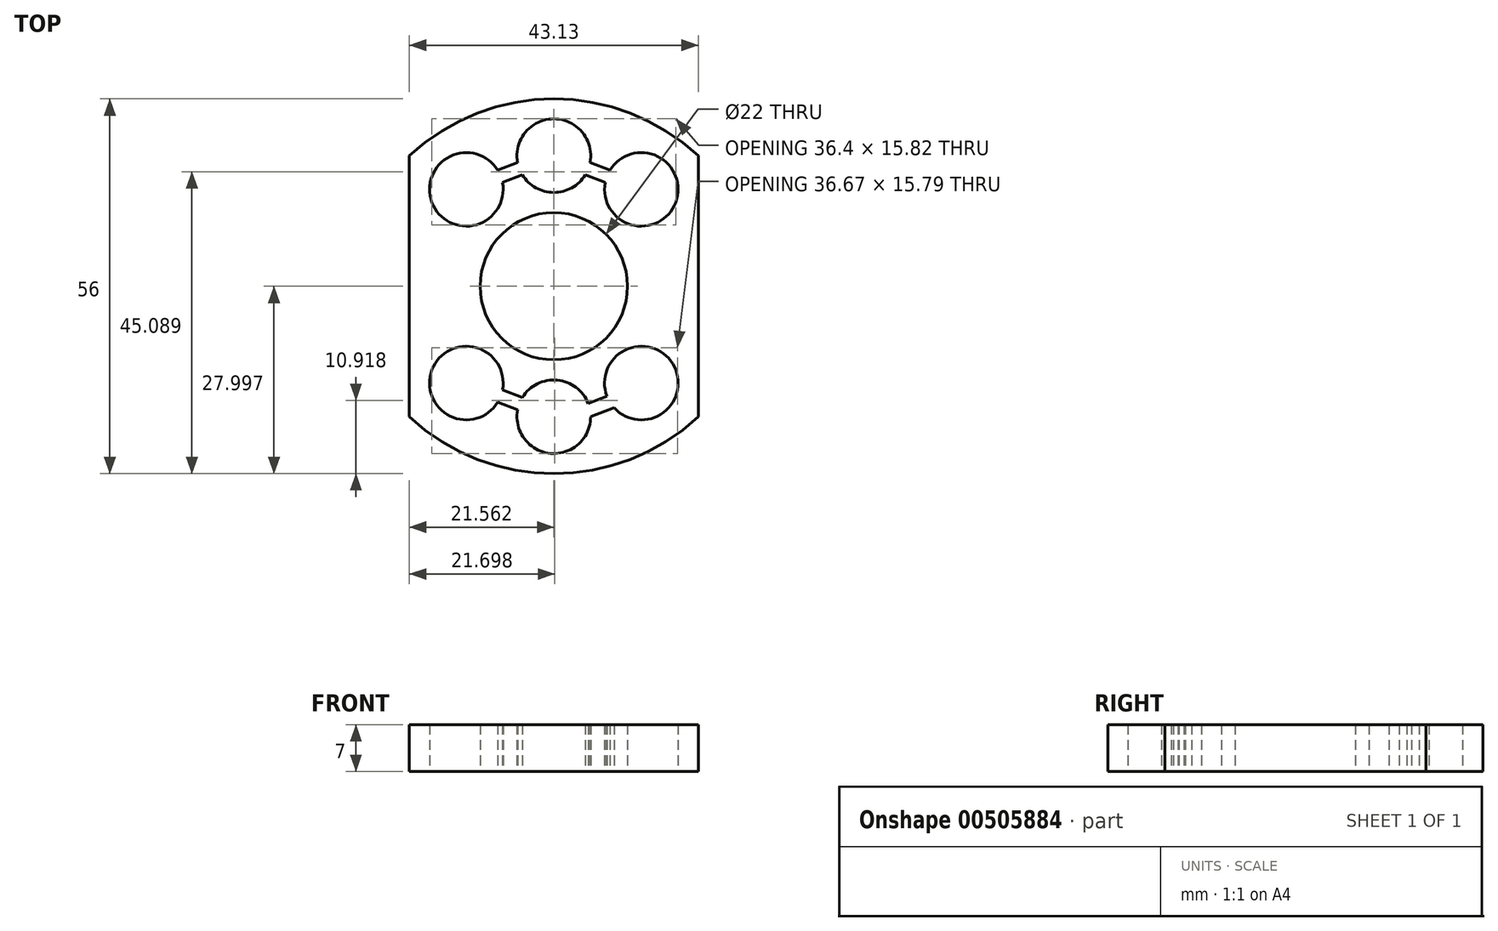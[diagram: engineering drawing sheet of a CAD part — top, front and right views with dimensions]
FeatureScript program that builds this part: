
annotation { "Feature Type Name" : "Feature", "Feature Type Description" : "" }
export const myFeature = defineFeature(function(context is Context, id is Id, definition is map)
    precondition{}
    {
        {
            var Q0;
            Q0=qCreatedBy(makeId("Top.planeOp"),FACE);
            var sketch = newSketch(context, id + "F0", { "sketchPlane" : qUnion([Q0])});
            skCircle(sketch, "E0", {"center": v(-13.1, -14.38) * mm, "radius": 5.5 * mm});
            skCircle(sketch, "E1", {"center": v(13.03, 14.57) * mm, "radius": 5.5 * mm});
            skCircle(sketch, "E2", {"center": v(-13.1, 14.57) * mm, "radius": 5.5 * mm});
            skCircle(sketch, "E3", {"center": v(-0.04, 19.6) * mm, "radius": 5.5 * mm});
            skCircle(sketch, "E4", {"center": v(-0.04, -19.4) * mm, "radius": 5.5 * mm});
            skCircle(sketch, "E5", {"center": v(13.03, -14.38) * mm, "radius": 5.5 * mm});
            skCircle(sketch, "E6", {"center": v(-0.04, 0.1) * mm, "radius": 11 * mm});
            skLineSegment(sketch, "E7", {"start": v(-7.7, 15.58) * mm, "end": v(-4.73, 16.72) * mm});
            skLineSegment(sketch, "E8", {"start": v(4.65, 16.72) * mm, "end": v(7.62, 15.58) * mm});
            skLineSegment(sketch, "E9", {"start": v(5.37, 18.59) * mm, "end": v(8.34, 17.45) * mm});
            skLineSegment(sketch, "E10", {"start": v(-8.42, 17.45) * mm, "end": v(-5.44, 18.59) * mm});
            skLineSegment(sketch, "E11", {"start": v(5.1, -17.43) * mm, "end": v(7.9, -16.35) * mm});
            skLineSegment(sketch, "E12", {"start": v(-8.42, -17.25) * mm, "end": v(-5.44, -18.4) * mm});
            skLineSegment(sketch, "E13", {"start": v(-7.7, -15.38) * mm, "end": v(-4.73, -16.53) * mm});
            skLineSegment(sketch, "E14", {"start": v(5.46, -19.4) * mm, "end": v(8.97, -18.08) * mm});
            skLineSegment(sketch, "E15", {"start": v(-21.6, 19.6) * mm, "end": v(-21.6, -19.4) * mm});
            skLineSegment(sketch, "E16", {"start": v(21.53, 19.6) * mm, "end": v(21.53, -19.4) * mm});
            skArc(sketch, "E17", {"start": v(21.53, 19.6) * mm, "mid": v(-0.04, 28.1) * mm, "end": v(-21.6, 19.6) * mm});
            skArc(sketch, "E18", {"start": v(-21.6, -19.4) * mm, "mid": v(-0.04, -27.9) * mm, "end": v(21.53, -19.4) * mm});
            skSolve(sketch);
        }
        {
            var Q0;
            Q0=makeQuery(id+"F0.imprint","IMPRINT",FACE,{"disambiguationData":[TD([[makeQuery(id+"F0.imprint","IMPRINT",EDGE,{"derivedFrom":sQuery(id+"F0.wireOp",EDGE,"E6")}),-1.0]])]});
            extrude(context, id + "F1", {"entities" : qUnion([Q0]), "depth" : 7 * mm});
        }
    });
